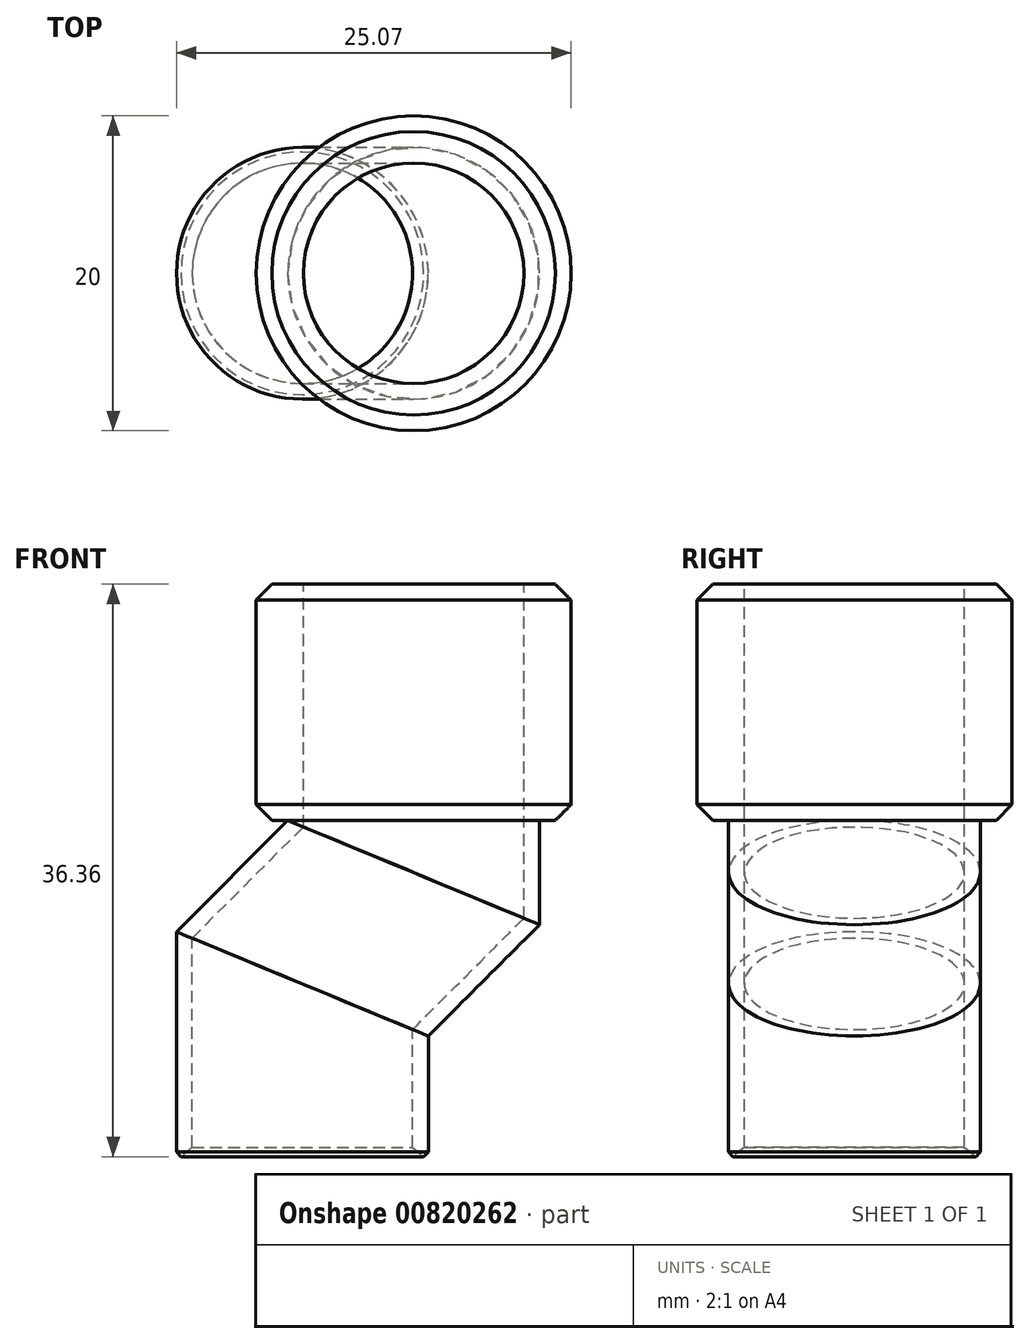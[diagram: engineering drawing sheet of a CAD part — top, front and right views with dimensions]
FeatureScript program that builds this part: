
annotation { "Feature Type Name" : "Feature", "Feature Type Description" : "" }
export const myFeature = defineFeature(function(context is Context, id is Id, definition is map)
    precondition{}
    {
        {
            var Q0;
            Q0=qCreatedBy(makeId("Top.planeOp"),FACE);
            var sketch = newSketch(context, id + "F0", { "sketchPlane" : qUnion([Q0])});
            skCircle(sketch, "E0", {"center": v(-39.1, 0) * mm, "radius": 8 * mm});
            skCircle(sketch, "E1", {"center": v(-39.1, 0) * mm, "radius": 7 * mm});
            skCircle(sketch, "E2", {"center": v(-32.03, 0) * mm, "radius": 10 * mm});
            skCircle(sketch, "E3", {"center": v(-32.03, 0) * mm, "radius": 8 * mm});
            skSolve(sketch);
        }
        {
            var Q0;
            Q0=qCreatedBy(makeId("Front.planeOp"),FACE);
            var sketch = newSketch(context, id + "F1", { "sketchPlane" : qUnion([Q0])});
            skLineSegment(sketch, "E4", {"start": v(-47.1, 0) * mm, "end": v(-47.1, 15) * mm});
            skLineSegment(sketch, "E5", {"start": v(-47.1, 15) * mm, "end": v(-40.03, 22.07) * mm});
            skLineSegment(sketch, "E6", {"start": v(-40.03, 22.07) * mm, "end": v(-40.03, 37.07) * mm});
            skSolve(sketch);
        }
        {
            var Q0;
            Q0=makeQuery(id+"F0.imprint","IMPRINT",FACE,{"disambiguationData":[TD([[makeQuery(id+"F0.imprint","IMPRINT",EDGE,{"derivedFrom":sQuery(id+"F0.wireOp",EDGE,"E0")}),1.0]])]});
            var Q1;
            Q1=sQuery(id+"F1.wireOp",EDGE,"E4");
            var Q2;
            Q2=sQuery(id+"F1.wireOp",EDGE,"E5");
            var Q3;
            Q3=sQuery(id+"F1.wireOp",EDGE,"E6");
            sweep(context, id + "F2", {"profiles" : qUnion([Q0]), "path" : qUnion([Q1, Q2, Q3])});
        }
        {
            var Q0;
            {var subQ0=sQuery(id+"F0.wireOp",EDGE,"E2");var subQ1=sQuery(id+"F0.wireOp",EDGE,"E0");var subQ2=makeQuery(id+"F0.imprint","INTERSECT",VERTEX,{"disambiguationData":[OD(0.0)],"derivedFrom":[subQ1,subQ0]});Q0=makeQuery(id+"F0.imprint","IMPRINT",FACE,{"disambiguationData":[TD([[makeQuery(id+"F0.imprint","IMPRINT",EDGE,{"disambiguationData":[TD([[subQ2,1.0]])],"derivedFrom":subQ1}),-1.0]])]});}
            var Q1;
            {var subQ0=sQuery(id+"F0.wireOp",EDGE,"E2");var subQ1=sQuery(id+"F0.wireOp",EDGE,"E1");var subQ2=makeQuery(id+"F0.imprint","INTERSECT",VERTEX,{"disambiguationData":[OD(0.0)],"derivedFrom":[subQ1,subQ0]});Q1=makeQuery(id+"F0.imprint","IMPRINT",FACE,{"disambiguationData":[TD([[makeQuery(id+"F0.imprint","IMPRINT",EDGE,{"disambiguationData":[TD([[subQ2,1.0]])],"derivedFrom":subQ1}),1.0]])]});}
            var Q2;
            {var subQ0=sQuery(id+"F0.wireOp",EDGE,"E2");var subQ1=sQuery(id+"F0.wireOp",EDGE,"E0");var subQ2=makeQuery(id+"F0.imprint","INTERSECT",VERTEX,{"disambiguationData":[OD(1.0)],"derivedFrom":[subQ1,subQ0]});Q2=makeQuery(id+"F0.imprint","IMPRINT",FACE,{"disambiguationData":[TD([[makeQuery(id+"F0.imprint","IMPRINT",EDGE,{"disambiguationData":[TD([[subQ2,-1.0]])],"derivedFrom":subQ1}),1.0]])]});}
            var Q3;
            {var subQ0=sQuery(id+"F0.wireOp",EDGE,"E2");var subQ1=sQuery(id+"F0.wireOp",EDGE,"E0");var subQ2=makeQuery(id+"F0.imprint","INTERSECT",VERTEX,{"disambiguationData":[OD(0.0)],"derivedFrom":[subQ1,subQ0]});Q3=makeQuery(id+"F0.imprint","IMPRINT",FACE,{"disambiguationData":[TD([[makeQuery(id+"F0.imprint","IMPRINT",EDGE,{"disambiguationData":[TD([[subQ2,1.0]])],"derivedFrom":subQ1}),1.0]])]});}
            extrude(context, id + "F3", {"entities" : qUnion([Q0, Q1, Q2, Q3]), "operationType" : NewBodyOperationType.ADD, "depth" : 37.07 * mm, "offsetDistance" : 25 * mm, "hasSecondDirection" : true, "secondDirectionOppositeDirection" : false, "secondDirectionDepth" : 22.07 * mm});
        }
        {
            var Q0;
            Q0=makeQuery(id+"F2.opSweep","CAP_EDGE",EDGE,{"disambiguationData":[OSD([sQuery(id+"F0.wireOp",EDGE,"E0"),sQuery(id+"F1.wireOp",VERTEX,"E4.start")])],"isStart":true});
            chamfer(context, id + "F4", {"entities" : qUnion([Q0]), "width" : 1 * mm, "tangentPropagation" : true});
        }
        {
            var Q0;
            Q0=makeQuery(id+"F4.opChamfer","BLEND_EDGE",EDGE,{"blendedFrom":[makeQuery(id+"F2.opSweep","CAP_EDGE",EDGE,{"disambiguationData":[OSD([sQuery(id+"F0.wireOp",EDGE,"E0"),sQuery(id+"F1.wireOp",VERTEX,"E4.start")])],"isStart":true}),makeQuery(id+"F2.opSweep","SWEPT_FACE",FACE,{"disambiguationData":[OSD([sQuery(id+"F0.wireOp",EDGE,"E1"),sQuery(id+"F1.wireOp",EDGE,"E4")])]})],"blendedInto":[makeQuery(id+"F2.opSweep","SWEPT_FACE",FACE,{"disambiguationData":[OSD([sQuery(id+"F0.wireOp",EDGE,"E1"),sQuery(id+"F1.wireOp",EDGE,"E4")])]})]});
            chamfer(context, id + "F5", {"entities" : qUnion([Q0]), "chamferType" : ChamferType.OFFSET_ANGLE, "width" : 1 * mm, "oppositeDirection" : false, "angle" : 85 * degree, "tangentPropagation" : true});
        }
        {
            var Q0;
            Q0=makeQuery(id+"F3.opExtrude","CAP_EDGE",EDGE,{"disambiguationData":[OSD([sQuery(id+"F0.wireOp",EDGE,"E2")])],"isStart":true});
            var Q1;
            Q1=makeQuery(id+"F3.opExtrude","CAP_EDGE",EDGE,{"disambiguationData":[OSD([sQuery(id+"F0.wireOp",EDGE,"E2")])],"isStart":false});
            chamfer(context, id + "F6", {"entities" : qUnion([Q0, Q1]), "width" : 1 * mm, "tangentPropagation" : true});
        }
    });
